# Revit family: 75731_PRESTO_Sanifirst Mitigeur thermostatique monotrou d'évier ou paillasse bébé Mastermix_FR
name_source: partatom
category: Appareils sanitaires
revit_build: Autodesk Revit 2018 (Build: 20190510_1515(x64)
units: mm (PartAtom-declared; Revit-internal decimal feet)

## family parameters
Basée sur le plan de construction = Non
Cote de connecteur circulaire = Utiliser le diamètre
Couper avec des vides une fois chargée = Non
Partagée = Non
Point de calcul de pièce = Non
Toujours verticalement = Oui
Type d'élément = Normal

## types (1)
- 75731 PRESTO Sanifirst Mitigeur thermostatique monotrou d'évier ou paillasse bébé Mastermix
    Adresse = 7, RUE RACINE - 92542 MONTROUGE CEDEX FRANCE
    Description = Robinet mitigeur thermostatique monotrou d'évier ou paillasse bébé Mastermix
    Diamètre arrivée d'eau = 12 mm  [stored 0.0393701 ft]
    Débit = Réglé usine 6L/min
    Fabricant = LES ROBINETSPRESTO S.A.
    Famille produit = Lavabo
    Flux arrivée d'eau = 0.0 L/s
    Garantie = 10 ans contre tout vice de fabrication.
3 ans pour la cartouche thermostatique
    Groupe produit = -
    Hauteur = 297 mm  [stored 0.974409 ft]
    Longueur = 220 mm  [stored 0.721785 ft]
    Matériau = PRESTO - Métal
    Matériau principal = Corps et volants ergonomiques rotatifs en zamak chromés
    Matériau secondaire = -
    Modèle = 75731 PRESTO Sanifirst Mitigeur thermostatique monotrou d'évier ou paillasse bébé Mastermix
    Pays fabricant = France
    Perte de charge arrivée d'eau = 0.0 Pa
    Poids = 0.00 kg
    Profondeur = 248 mm  [stored 0.813648 ft]
    Raccordement = G 3/8"
    SKU produit = 75731
    URL = http://www.prestodatashare.com
    Variantes = 75731
    Visibilité flexible = Oui

note: [stored X ft] marks values corroborated as IEEE doubles in the binary element streams (Revit-internal decimal feet)
